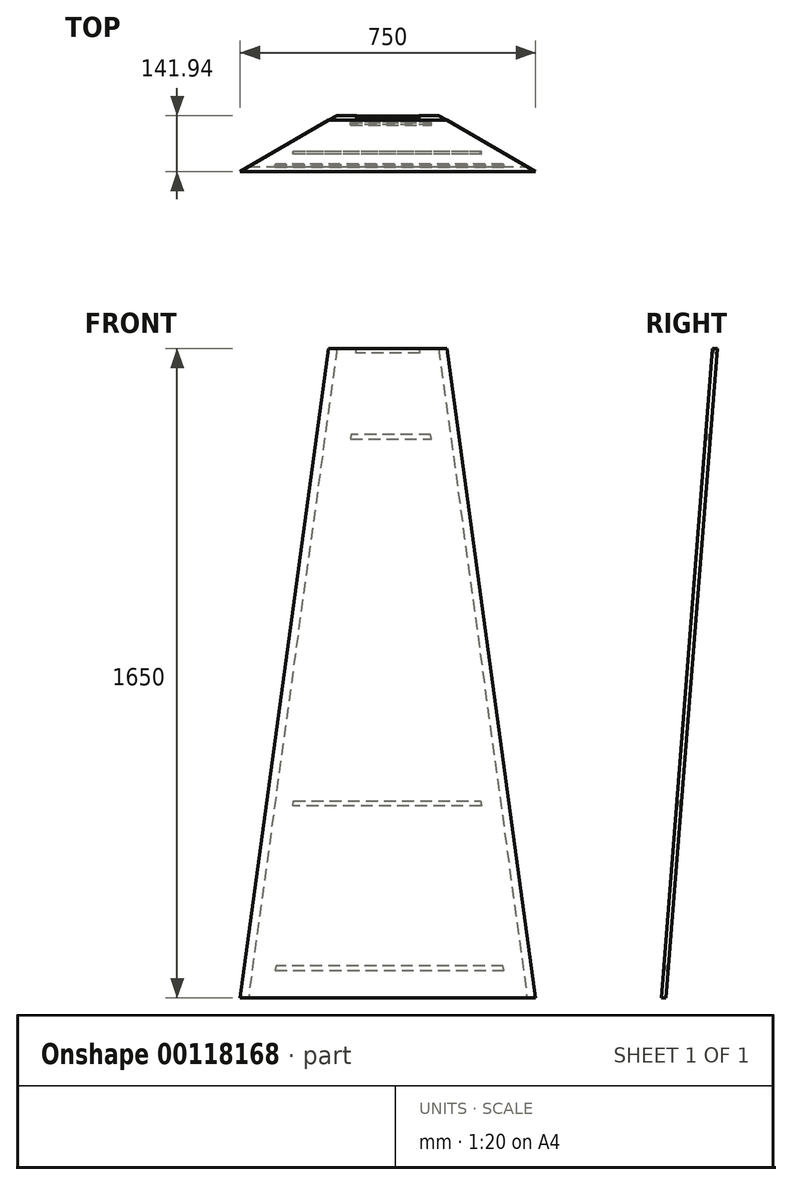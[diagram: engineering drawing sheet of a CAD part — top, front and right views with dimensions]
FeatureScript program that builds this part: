
annotation { "Feature Type Name" : "Feature", "Feature Type Description" : "" }
export const myFeature = defineFeature(function(context is Context, id is Id, definition is map)
    precondition{}
    {
        {
            var Q0;
            Q0=qCreatedBy(makeId("Front.planeOp"),FACE);
            var sketch = newSketch(context, id + "F0", { "sketchPlane" : qUnion([Q0])});
            skLineSegment(sketch, "E0", {"start": v(-375, 0) * mm, "end": v(375, 0) * mm});
            skLineSegment(sketch, "E1", {"start": v(0, 0) * mm, "end": v(0, 1650) * mm});
            skLineSegment(sketch, "E2", {"start": v(-150, 1650) * mm, "end": v(150, 1650) * mm});
            skSolve(sketch);
        }
        {
            var Q0;
            Q0=sQuery(id+"F0.wireOp",EDGE,"E2");
            cPoint(context, id + "F1", {"entities" : qUnion([Q0]), "parameter" : 0.5});
        }
        {
            var Q0;
            Q0=qCreatedBy(id+"F1",VERTEX);
            var Q1;
            Q1=sQuery(id+"F0.wireOp",EDGE,"E1");
            cPlane(context, id + "F2", {"entities" : qUnion([Q0, Q1]), "cplaneType" : CPlaneType.LINE_POINT, "offset" : 25 * mm, "width" : 150 * mm, "height" : 150 * mm});
        }
        {
            var Q0;
            Q0=qCreatedBy(makeId("Top.planeOp"),FACE);
            var sketch = newSketch(context, id + "F3", { "sketchPlane" : qUnion([Q0])});
            skCircle(sketch, "E3.cCircle", {"center": v(0, 0) * mm, "radius": 216.5 * mm, "construction": true});
            skLineSegment(sketch, "E3.0", {"start": v(375, -216.5) * mm, "end": v(-375, -216.5) * mm});
            skLineSegment(sketch, "E3.1", {"start": v(-375, -216.5) * mm, "end": v(0, 433.01) * mm});
            skLineSegment(sketch, "E3.2", {"start": v(0, 433.01) * mm, "end": v(375, -216.5) * mm});
            skPoint(sketch, "E3.0.midPoint", {"position": v(0, -216.5) * mm});
            skSolve(sketch);
        }
        {
            var Q0;
            Q0=qCreatedBy(id+"F2.planeOp",FACE);
            var sketch = newSketch(context, id + "F4", { "sketchPlane" : qUnion([Q0])});
            skCircle(sketch, "E4.cCircle", {"center": v(0, 0) * mm, "radius": 86.6 * mm, "construction": true});
            skLineSegment(sketch, "E4.0", {"start": v(150, -86.6) * mm, "end": v(-150, -86.6) * mm});
            skLineSegment(sketch, "E4.1", {"start": v(-150, -86.6) * mm, "end": v(0, 173.2) * mm});
            skLineSegment(sketch, "E4.2", {"start": v(0, 173.2) * mm, "end": v(150, -86.6) * mm});
            skPoint(sketch, "E4.0.midPoint", {"position": v(0, -86.6) * mm});
            skSolve(sketch);
        }
        {
            var Q0;
            Q0=makeQuery(id+"F3.imprint","IMPRINT",FACE,{"disambiguationData":[TD([[makeQuery(id+"F3.imprint","IMPRINT",EDGE,{"derivedFrom":sQuery(id+"F3.wireOp",EDGE,"E3.0")}),-1.0]])]});
            var Q1;
            Q1=makeQuery(id+"F4.imprint","IMPRINT",FACE,{"disambiguationData":[TD([[makeQuery(id+"F4.imprint","IMPRINT",EDGE,{"derivedFrom":sQuery(id+"F4.wireOp",EDGE,"E4.0")}),-1.0]])]});
            loft(context, id + "F5", {"sheetProfilesArray" : [{ "sheetProfileEntities" : qUnion([Q0]) }, { "sheetProfileEntities" : qUnion([Q1]) }]});
        }
        {
            var Q0;
            {var subQ0=sQuery(id+"F4.wireOp",EDGE,"E4.0");var subQ1=sQuery(id+"F4.wireOp",EDGE,"E4.1");var subQ2=sQuery(id+"F4.wireOp",EDGE,"E4.2");var subQ3=sQuery(id+"F3.wireOp",EDGE,"E3.0");var subQ4=sQuery(id+"F3.wireOp",EDGE,"E3.1");var subQ5=sQuery(id+"F3.wireOp",EDGE,"E3.2");Q0=makeQuery(id+"F5.opLoft","SWEPT_FACE",FACE,{"disambiguationData":[OSD([subQ3,subQ4,subQ5,subQ0,subQ1,subQ2]),TDD([makeQuery(id+"F3.imprint","INTERSECT",VERTEX,{"derivedFrom":[subQ3,subQ5]}),makeQuery(id+"F3.imprint","INTERSECT",VERTEX,{"derivedFrom":[subQ3,subQ4]}),makeQuery(id+"F3.imprint","IMPRINT",EDGE,{"derivedFrom":subQ3}),makeQuery(id+"F4.imprint","INTERSECT",VERTEX,{"derivedFrom":[subQ0,subQ2]}),makeQuery(id+"F4.imprint","INTERSECT",VERTEX,{"derivedFrom":[subQ0,subQ1]}),makeQuery(id+"F4.imprint","IMPRINT",EDGE,{"derivedFrom":subQ0})])]});}
            cPlane(context, id + "F6", {"entities" : qUnion([Q0]), "cplaneType" : CPlaneType.OFFSET, "offset" : 12 * mm, "oppositeDirection" : true, "width" : 150 * mm, "height" : 150 * mm});
        }
        {
            var Q0;
            Q0=qCreatedBy(id+"F6.planeOp",FACE);
            var sketch = newSketch(context, id + "F7", { "sketchPlane" : qUnion([Q0])});
            skCircle(sketch, "E5", {"center": v(0, 812.97) * mm, "radius": 960.24 * mm});
            skSolve(sketch);
        }
        {
            var Q0;
            Q0=qSketchRegion(id+"F7",true);
            extrude(context, id + "F8", {"entities" : qUnion([Q0]), "operationType" : NewBodyOperationType.REMOVE, "endBound" : BoundingType.THROUGH_ALL, "oppositeDirection" : true, "depth" : 25 * mm});
        }
        {
            var Q0;
            Q0=makeQuery(id+"F5.opLoft","CAP_FACE",FACE,{"disambiguationData":[OSD([makeQuery(id+"F4.imprint","IMPRINT",FACE,{"disambiguationData":[TD([[makeQuery(id+"F4.imprint","IMPRINT",EDGE,{"derivedFrom":sQuery(id+"F4.wireOp",EDGE,"E4.0")}),-1.0]])]})])],"isStart":true});
            var sketch = newSketch(context, id + "F9", { "sketchPlane" : qUnion([Q0])});
            skLineSegment(sketch, "E6", {"start": v(150, -86.6) * mm, "end": v(129.15, -74.57) * mm});
            skLineSegment(sketch, "E7", {"start": v(-150, -86.6) * mm, "end": v(-129.15, -74.57) * mm});
            skLineSegment(sketch, "E8", {"start": v(129.15, -74.57) * mm, "end": v(70, -40.41) * mm, "construction": true});
            skLineSegment(sketch, "E9", {"start": v(129.15, -74.57) * mm, "end": v(104.15, -31.26) * mm, "construction": true});
            skLineSegment(sketch, "E10", {"start": v(104.15, -31.26) * mm, "end": v(70, -40.41) * mm, "construction": true});
            skLineSegment(sketch, "E11.MirrorCS", {"start": v(79.15, -74.57) * mm, "end": v(70, -40.41) * mm, "construction": true});
            skLineSegment(sketch, "E12.MirrorCS", {"start": v(129.15, -74.57) * mm, "end": v(79.15, -74.57) * mm, "construction": true});
            skSolve(sketch);
        }
        {
            var Q0;
            Q0=makeQuery(id+"F5.opLoft","SWEPT_EDGE",EDGE,{"disambiguationData":[OSD([sQuery(id+"F3.wireOp",EDGE,"E3.0"),sQuery(id+"F3.wireOp",EDGE,"E3.1"),sQuery(id+"F4.wireOp",EDGE,"E4.0"),sQuery(id+"F4.wireOp",EDGE,"E4.1")])]});
            var Q1;
            Q1=sQuery(id+"F9.wireOp",EDGE,"E7");
            cPlane(context, id + "F10", {"entities" : qUnion([Q0, Q1]), "cplaneType" : CPlaneType.LINE_ANGLE, "offset" : 25 * mm, "angle" : 0 * degree, "width" : 150 * mm, "height" : 150 * mm});
        }
        {
            var Q0;
            Q0=makeQuery(id+"F5.opLoft","SWEPT_EDGE",EDGE,{"disambiguationData":[OSD([sQuery(id+"F3.wireOp",EDGE,"E3.0"),sQuery(id+"F3.wireOp",EDGE,"E3.2"),sQuery(id+"F4.wireOp",EDGE,"E4.0"),sQuery(id+"F4.wireOp",EDGE,"E4.2")])]});
            var Q1;
            Q1=sQuery(id+"F9.wireOp",EDGE,"E6");
            cPlane(context, id + "F11", {"entities" : qUnion([Q0, Q1]), "cplaneType" : CPlaneType.LINE_ANGLE, "offset" : 25 * mm, "angle" : 0 * degree, "width" : 150 * mm, "height" : 150 * mm});
        }
        {
            var Q0;
            Q0=qCreatedBy(id+"F11.planeOp",FACE);
            var sketch = newSketch(context, id + "F12", { "sketchPlane" : qUnion([Q0])});
            skCircle(sketch, "E13", {"center": v(304.07, 817.21) * mm, "radius": 870.23 * mm});
            skSolve(sketch);
        }
        {
            var Q0;
            Q0=qSketchRegion(id+"F12",true);
            extrude(context, id + "F13", {"entities" : qUnion([Q0]), "operationType" : NewBodyOperationType.REMOVE, "oppositeDirection" : true, "depth" : 25 * mm});
        }
        {
            var Q0;
            Q0=qCreatedBy(id+"F10.planeOp",FACE);
            var sketch = newSketch(context, id + "F14", { "sketchPlane" : qUnion([Q0])});
            skCircle(sketch, "E14", {"center": v(291.65, 811.12) * mm, "radius": 892.94 * mm});
            skSolve(sketch);
        }
        {
            var Q0;
            Q0=qSketchRegion(id+"F14",true);
            extrude(context, id + "F15", {"entities" : qUnion([Q0]), "operationType" : NewBodyOperationType.REMOVE, "depth" : 25 * mm});
        }
        {
            var Q0;
            Q0=qCreatedBy(makeId("Front.planeOp"),FACE);
            var sketch = newSketch(context, id + "F16", { "sketchPlane" : qUnion([Q0])});
            skLineSegment(sketch, "E15.0.0", {"start": v(-354.15, 0) * mm, "end": v(-129.15, 1650) * mm, "construction": true});
            skLineSegment(sketch, "E15.0.1", {"start": v(-129.15, 1650) * mm, "end": v(129.15, 1650) * mm});
            skLineSegment(sketch, "E15.0.2", {"start": v(129.15, 1650) * mm, "end": v(354.15, 0) * mm, "construction": true});
            skLineSegment(sketch, "E16.0.1", {"start": v(-150, 1650) * mm, "end": v(-375, 0) * mm, "construction": true});
            skLineSegment(sketch, "E16.0.3", {"start": v(375, 0) * mm, "end": v(150, 1650) * mm, "construction": true});
            skLineSegment(sketch, "E17", {"start": v(0, 0) * mm, "end": v(0, 50) * mm, "construction": true});
            skLineSegment(sketch, "E18", {"start": v(0, 1400) * mm, "end": v(0, 1650) * mm, "construction": true});
            skLineSegment(sketch, "E19", {"start": v(0, 1400) * mm, "end": v(0, 500) * mm, "construction": true});
            skLineSegment(sketch, "E20", {"start": v(0, 500) * mm, "end": v(0, 50) * mm, "construction": true});
            skLineSegment(sketch, "E21", {"start": v(205.9, 500) * mm, "end": v(-205.9, 500) * mm});
            skLineSegment(sketch, "E22", {"start": v(-205.9, 500) * mm, "end": v(-83.17, 1400) * mm});
            skLineSegment(sketch, "E23", {"start": v(-83.17, 1400) * mm, "end": v(83.17, 1400) * mm});
            skLineSegment(sketch, "E24", {"start": v(83.17, 1400) * mm, "end": v(205.9, 500) * mm});
            skSolve(sketch);
        }
        {
            var Q0;
            Q0=qCreatedBy(makeId("Front.planeOp"),FACE);
            var sketch = newSketch(context, id + "F17", { "sketchPlane" : qUnion([Q0])});
            skLineSegment(sketch, "E25.0", {"start": v(129.15, 1650) * mm, "end": v(79.15, 1650) * mm, "construction": true});
            skLineSegment(sketch, "E26.0", {"start": v(375, 0) * mm, "end": v(150, 1650) * mm, "construction": true});
            skLineSegment(sketch, "E27.0", {"start": v(129.15, 1650) * mm, "end": v(354.15, 0) * mm, "construction": true});
            skLineSegment(sketch, "E28", {"start": v(354.15, 0) * mm, "end": v(304.15, 0) * mm, "construction": true});
            skLineSegment(sketch, "E29.0", {"start": v(-354.15, 0) * mm, "end": v(-129.15, 1650) * mm, "construction": true});
            skLineSegment(sketch, "E30.0", {"start": v(-150, 1650) * mm, "end": v(-375, 0) * mm, "construction": true});
            skLineSegment(sketch, "E31", {"start": v(-354.15, 0) * mm, "end": v(-304.15, 0) * mm, "construction": true});
            skLineSegment(sketch, "E32", {"start": v(-129.15, 1650) * mm, "end": v(-79.15, 1650) * mm, "construction": true});
            skLineSegment(sketch, "E33", {"start": v(79.15, 1650) * mm, "end": v(304.15, 0) * mm, "construction": true});
            skPoint(sketch, "E34.0", {"position": v(0, 50) * mm});
            skPoint(sketch, "E35.0", {"position": v(0, 500) * mm});
            skPoint(sketch, "E36.0", {"position": v(0, 1400) * mm});
            skLineSegment(sketch, "E37", {"start": v(110.51, 1420) * mm, "end": v(-94.79, 1420) * mm});
            skLineSegment(sketch, "E38", {"start": v(-94.79, 1420) * mm, "end": v(-93.15, 1432) * mm});
            skLineSegment(sketch, "E39", {"start": v(-93.15, 1432) * mm, "end": v(108.88, 1432) * mm});
            skLineSegment(sketch, "E40", {"start": v(108.88, 1432) * mm, "end": v(110.51, 1420) * mm});
            skLineSegment(sketch, "E41", {"start": v(79.15, 1650) * mm, "end": v(-79.15, 1650) * mm});
            skLineSegment(sketch, "E42", {"start": v(-79.15, 1650) * mm, "end": v(-80.79, 1638) * mm});
            skLineSegment(sketch, "E43", {"start": v(-80.79, 1638) * mm, "end": v(80.79, 1638) * mm});
            skLineSegment(sketch, "E44", {"start": v(80.79, 1638) * mm, "end": v(79.15, 1650) * mm});
            skLineSegment(sketch, "E45", {"start": v(235.97, 500) * mm, "end": v(-239.44, 500) * mm});
            skLineSegment(sketch, "E46", {"start": v(-239.44, 500) * mm, "end": v(-241.08, 488) * mm});
            skLineSegment(sketch, "E47", {"start": v(-241.08, 488) * mm, "end": v(237.6, 488) * mm});
            skLineSegment(sketch, "E48", {"start": v(237.6, 488) * mm, "end": v(235.97, 500) * mm});
            skLineSegment(sketch, "E49", {"start": v(294.6, 70) * mm, "end": v(-286.22, 70) * mm});
            skLineSegment(sketch, "E50", {"start": v(-286.22, 70) * mm, "end": v(-284.58, 82) * mm});
            skLineSegment(sketch, "E51", {"start": v(-284.58, 82) * mm, "end": v(292.97, 82) * mm});
            skLineSegment(sketch, "E52", {"start": v(292.97, 82) * mm, "end": v(294.6, 70) * mm});
            skLineSegment(sketch, "E53", {"start": v(-79.15, 1650) * mm, "end": v(-304.15, 0) * mm, "construction": true});
            skSolve(sketch);
        }
        {
            var Q0;
            Q0=makeQuery(id+"F8.boolean.opBoolean","COPY",FACE,{"derivedFrom":makeQuery(id+"F8.opExtrude","CAP_FACE",FACE,{"disambiguationData":[OSD([sQuery(id+"F7.wireOp",EDGE,"E5")])],"isStart":true})});
            cPlane(context, id + "F18", {"entities" : qUnion([Q0]), "cplaneType" : CPlaneType.OFFSET, "offset" : 6 * mm, "oppositeDirection" : true, "width" : 150 * mm, "height" : 150 * mm});
        }
        {
            var Q0;
            Q0=makeQuery(id+"F17.imprint","IMPRINT",FACE,{"disambiguationData":[TD([[makeQuery(id+"F17.imprint","IMPRINT",EDGE,{"derivedFrom":sQuery(id+"F17.wireOp",EDGE,"E41")}),1.0]])]});
            var Q1;
            Q1=makeQuery(id+"F17.imprint","IMPRINT",FACE,{"disambiguationData":[TD([[makeQuery(id+"F17.imprint","IMPRINT",EDGE,{"derivedFrom":sQuery(id+"F17.wireOp",EDGE,"E37")}),-1.0]])]});
            var Q2;
            Q2=makeQuery(id+"F17.imprint","IMPRINT",FACE,{"disambiguationData":[TD([[makeQuery(id+"F17.imprint","IMPRINT",EDGE,{"derivedFrom":sQuery(id+"F17.wireOp",EDGE,"E45")}),1.0]])]});
            var Q3;
            Q3=makeQuery(id+"F17.imprint","IMPRINT",FACE,{"disambiguationData":[TD([[makeQuery(id+"F17.imprint","IMPRINT",EDGE,{"derivedFrom":sQuery(id+"F17.wireOp",EDGE,"E49")}),-1.0]])]});
            var Q4;
            Q4=qCreatedBy(id+"F18.planeOp",FACE);
            extrude(context, id + "F19", {"entities" : qUnion([Q0, Q1, Q2, Q3]), "operationType" : NewBodyOperationType.REMOVE, "endBound" : BoundingType.UP_TO_SURFACE, "endBoundEntityFace" : qUnion([Q4]), "depth" : 25 * mm});
        }
    });
